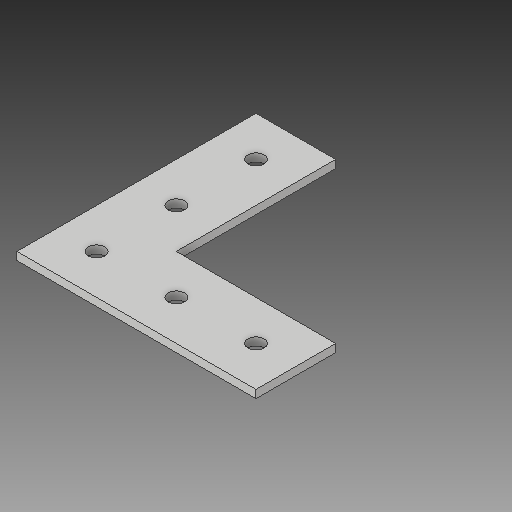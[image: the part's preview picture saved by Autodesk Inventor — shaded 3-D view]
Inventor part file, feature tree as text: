
AUTODESK INVENTOR PART (.ipt)
format: ipt  version: 2018 (Build 220112000, 112)  size: 121,856 bytes
history: native  units: in
note: dims shown in document units (in); Inventor stores cm internally (conversion verified against a paired STEP export)
features: extrude x1, sketch x1
ambient origin geometry x8: Origin, YZ Plane, XZ Plane, XY Plane, X Axis, Y Axis, Z Axis, Center Point
bodies: Solid1 (feature_tree)
feature tree (2):
  extrude  "Extrusion1"  Depth=1.0in
  sketch  "Sketch1"  dims[d0=0.0in d1=1.0in d2=3.0in d3=2.0in d4=1.0in d5=0.5in d6=0.5in d7=0.5in d8=0.5in d9=1.0in d10=1.0in d11=0.2031in d12=0.2031in d13=0.2031in d14=0.2031in d15=0.2031in d16=0.5in d17=0.5in d18=0.5in d19=1.0in d20=0.5in d21=0.1in d22=0.0in]
